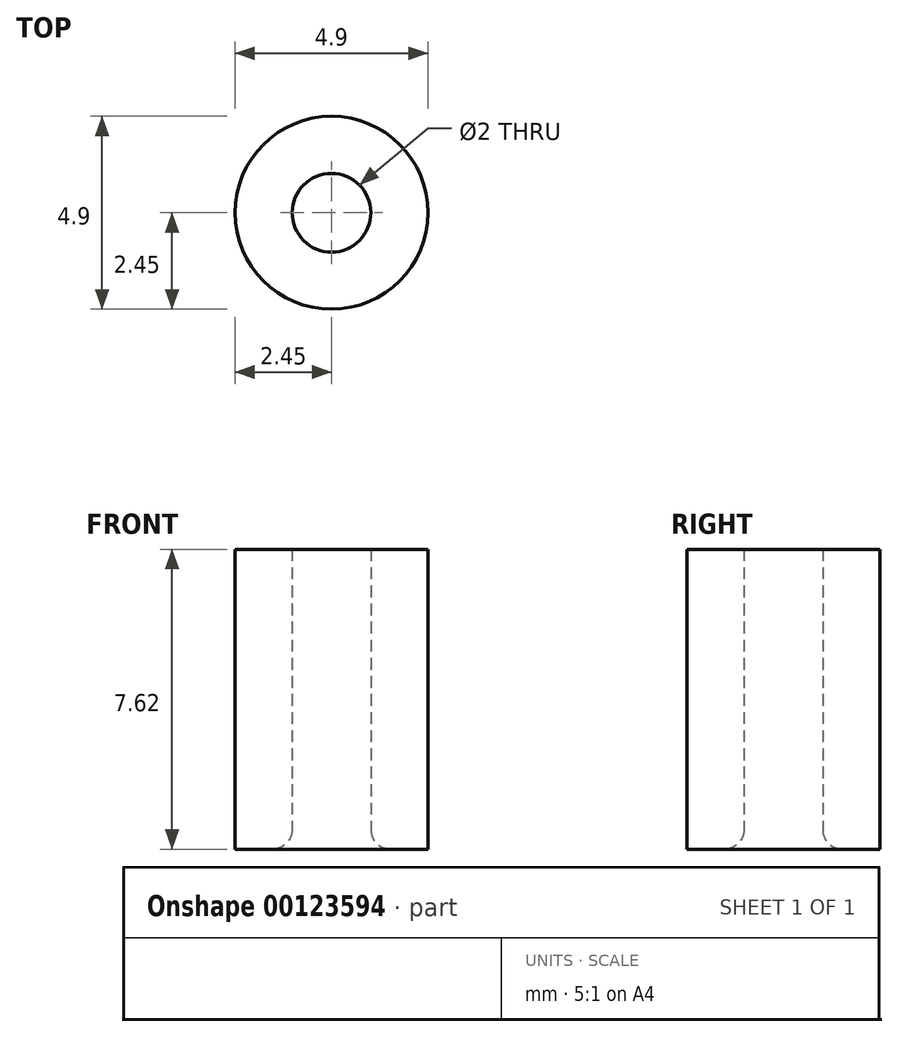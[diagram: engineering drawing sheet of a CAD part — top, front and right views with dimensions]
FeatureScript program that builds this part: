
annotation { "Feature Type Name" : "Feature", "Feature Type Description" : "" }
export const myFeature = defineFeature(function(context is Context, id is Id, definition is map)
    precondition{}
    {
        {
            var Q0;
            Q0=qCreatedBy(makeId("Top.planeOp"),FACE);
            var sketch = newSketch(context, id + "F0", { "sketchPlane" : qUnion([Q0])});
            skCircle(sketch, "E0", {"center": v(0, 0) * mm, "radius": 2.45 * mm});
            skCircle(sketch, "E1", {"center": v(0, 0) * mm, "radius": 1 * mm});
            skSolve(sketch);
        }
        {
            var Q0;
            Q0 = qSketchRegion(id + "F0", true);
            extrude(context, id + "F1", {"entities" : qUnion([Q0]), "depth" : 7.62 * mm});
        }
        {
            var Q0;
            Q0=makeQuery(id+"F1.opExtrude","CAP_EDGE",EDGE,{"disambiguationData":[OSD([sQuery(id+"F0.wireOp",EDGE,"E1")])],"isStart":true});
            fillet(context, id + "F2", {"entities" : qUnion([Q0]), "radius" : .5 * mm, "tangentPropagation" : true, "allowEdgeOverflow" : false});
        }
    });
